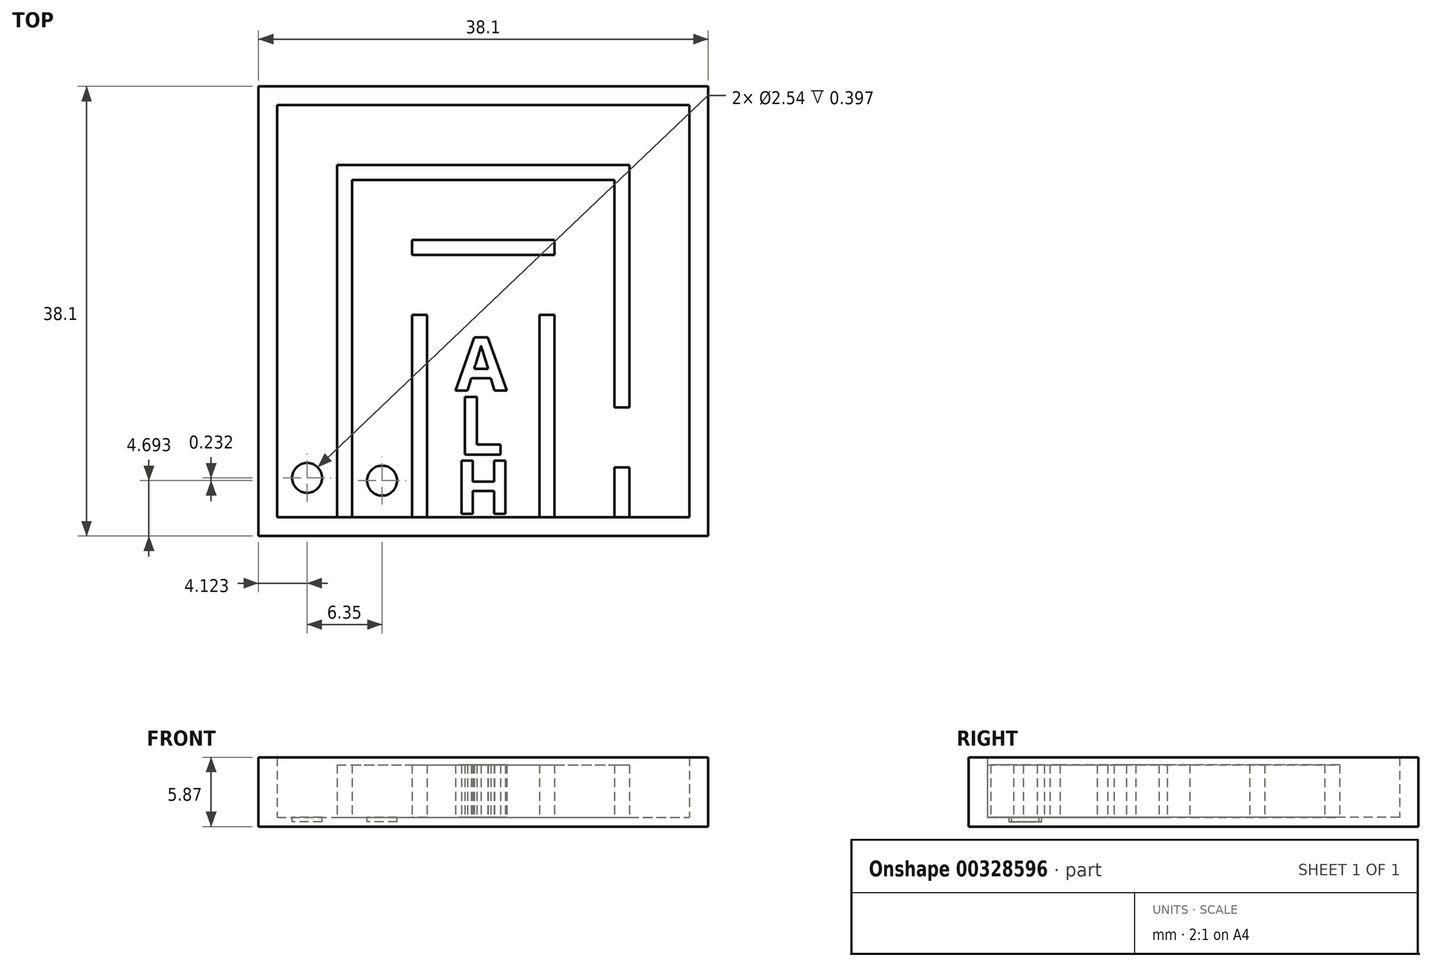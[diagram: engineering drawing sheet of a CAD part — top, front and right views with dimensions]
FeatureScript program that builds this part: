
annotation { "Feature Type Name" : "Feature", "Feature Type Description" : "" }
export const myFeature = defineFeature(function(context is Context, id is Id, definition is map)
    precondition{}
    {
        {
            var Q0;
            Q0=qCreatedBy(makeId("Top.planeOp"),FACE);
            var sketch = newSketch(context, id + "F0", { "sketchPlane" : qUnion([Q0])});
            skLineSegment(sketch, "E0.bottom", {"start": v(-17.72, 13.91) * mm, "end": v(20.38, 13.91) * mm});
            skLineSegment(sketch, "E0.top", {"start": v(-17.72, -24.19) * mm, "end": v(20.38, -24.19) * mm});
            skLineSegment(sketch, "E0.left", {"start": v(-17.72, 13.91) * mm, "end": v(-17.72, -24.19) * mm});
            skLineSegment(sketch, "E0.right", {"start": v(20.38, 13.91) * mm, "end": v(20.38, -24.19) * mm});
            skSolve(sketch);
        }
        {
            var Q0;
            Q0=makeQuery(id+"F0.imprint","IMPRINT",FACE,{"disambiguationData":[TD([[makeQuery(id+"F0.imprint","IMPRINT",EDGE,{"derivedFrom":sQuery(id+"F0.wireOp",EDGE,"E0.bottom")}),-1.0]])]});
            extrude(context, id + "F1", {"entities" : qUnion([Q0]), "depth" : 0.8 * mm});
        }
        {
            var Q0;
            Q0=makeQuery(id+"F1.opExtrude","CAP_FACE",FACE,{"disambiguationData":[OSD([sQuery(id+"F0.wireOp",EDGE,"E0.bottom"),sQuery(id+"F0.wireOp",EDGE,"E0.top"),sQuery(id+"F0.wireOp",EDGE,"E0.left"),sQuery(id+"F0.wireOp",EDGE,"E0.right")])],"isStart":false});
            var sketch = newSketch(context, id + "F2", { "sketchPlane" : qUnion([Q0])});
            skLineSegment(sketch, "E1.0", {"start": v(-16.14, 12.33) * mm, "end": v(18.79, 12.33) * mm});
            skLineSegment(sketch, "E1.1", {"start": v(-16.14, 12.33) * mm, "end": v(-16.14, -22.6) * mm});
            skLineSegment(sketch, "E1.2", {"start": v(-16.14, -22.6) * mm, "end": v(18.79, -22.6) * mm});
            skLineSegment(sketch, "E1.3", {"start": v(18.79, 12.33) * mm, "end": v(18.79, -22.6) * mm});
            skSolve(sketch);
        }
        {
            var Q0;
            Q0=makeQuery(id+"F2.imprint","IMPRINT",FACE,{"disambiguationData":[TD([[makeQuery(id+"F2.imprint","IMPRINT",EDGE,{"derivedFrom":sQuery(id+"F2.wireOp",EDGE,"E1.0")}),1.0]])]});
            extrude(context, id + "F3", {"entities" : qUnion([Q0]), "operationType" : NewBodyOperationType.ADD, "depth" : 5.08 * mm});
        }
        {
            var Q0;
            Q0=makeQuery(id+"F1.opExtrude","CAP_FACE",FACE,{"disambiguationData":[OSD([sQuery(id+"F0.wireOp",EDGE,"E0.bottom"),sQuery(id+"F0.wireOp",EDGE,"E0.top"),sQuery(id+"F0.wireOp",EDGE,"E0.left"),sQuery(id+"F0.wireOp",EDGE,"E0.right")])],"isStart":false});
            var sketch = newSketch(context, id + "F4", { "sketchPlane" : qUnion([Q0])});
            skLineSegment(sketch, "E2.bottom", {"start": v(-11.06, -22.6) * mm, "end": v(-9.79, -22.6) * mm});
            skLineSegment(sketch, "E2.top", {"start": v(-11.06, 7.25) * mm, "end": v(-9.79, 7.25) * mm});
            skLineSegment(sketch, "E2.left", {"start": v(-11.06, -22.6) * mm, "end": v(-11.06, 7.25) * mm});
            skLineSegment(sketch, "E2.right", {"start": v(-9.79, -22.6) * mm, "end": v(-9.79, 5.98) * mm});
            skLineSegment(sketch, "E3.bottom", {"start": v(-9.79, 7.25) * mm, "end": v(13.7, 7.25) * mm});
            skLineSegment(sketch, "E3.top", {"start": v(-9.79, 5.98) * mm, "end": v(12.44, 5.98) * mm});
            skLineSegment(sketch, "E3.right", {"start": v(13.7, 7.25) * mm, "end": v(13.7, 5.98) * mm});
            skLineSegment(sketch, "E4.left", {"start": v(18.79, 5.98) * mm, "end": v(18.79, 0.9) * mm});
            skLineSegment(sketch, "E5.right", {"start": v(7.36, -0.37) * mm, "end": v(7.36, 0.9) * mm});
            skLineSegment(sketch, "E6.top", {"start": v(12.44, -13.3) * mm, "end": v(13.7, -13.3) * mm});
            skLineSegment(sketch, "E6.left", {"start": v(12.44, 5.98) * mm, "end": v(12.44, -13.3) * mm});
            skLineSegment(sketch, "E6.right", {"start": v(13.7, 5.98) * mm, "end": v(13.7, -13.3) * mm});
            skLineSegment(sketch, "E7.bottom", {"start": v(12.44, -22.6) * mm, "end": v(13.7, -22.6) * mm});
            skLineSegment(sketch, "E7.top", {"start": v(12.44, -18.39) * mm, "end": v(13.7, -18.39) * mm});
            skLineSegment(sketch, "E7.left", {"start": v(12.44, -22.6) * mm, "end": v(12.44, -18.39) * mm});
            skLineSegment(sketch, "E7.right", {"start": v(13.7, -22.6) * mm, "end": v(13.7, -18.39) * mm});
            skLineSegment(sketch, "E8.bottom", {"start": v(-3.44, -22.6) * mm, "end": v(-4.7, -22.6) * mm});
            skLineSegment(sketch, "E8.top", {"start": v(-3.44, -5.45) * mm, "end": v(-4.7, -5.45) * mm});
            skLineSegment(sketch, "E8.left", {"start": v(-3.44, -22.6) * mm, "end": v(-3.44, -5.45) * mm});
            skLineSegment(sketch, "E8.right", {"start": v(-4.7, -22.6) * mm, "end": v(-4.7, -5.45) * mm});
            skLineSegment(sketch, "E9.trimOffspring", {"start": v(12.44, 5.98) * mm, "end": v(-0.53, 5.98) * mm});
            skLineSegment(sketch, "E10", {"start": v(-4.7, 0.9) * mm, "end": v(-4.7, -0.37) * mm});
            skLineSegment(sketch, "E11", {"start": v(-4.7, -0.37) * mm, "end": v(7.36, -0.37) * mm});
            skLineSegment(sketch, "E12", {"start": v(-4.7, 0.9) * mm, "end": v(7.36, 0.9) * mm});
            skLineSegment(sketch, "E13.bottom", {"start": v(6.09, -5.45) * mm, "end": v(7.36, -5.45) * mm});
            skLineSegment(sketch, "E13.top", {"start": v(6.09, -22.6) * mm, "end": v(7.36, -22.6) * mm});
            skLineSegment(sketch, "E13.left", {"start": v(6.09, -5.45) * mm, "end": v(6.09, -22.6) * mm});
            skLineSegment(sketch, "E13.right", {"start": v(7.36, -5.45) * mm, "end": v(7.36, -22.6) * mm});
            skLineSegment(sketch, "E14", {"start": v(-16.14, -22.6) * mm, "end": v(-11.06, -22.6) * mm});
            skCircle(sketch, "E15", {"center": v(-13.6, -19.26) * mm, "radius": 1.27 * mm});
            skPoint(sketch, "E15.centerSnap0", {"position": v(-13.6, -22.6) * mm});
            skLineSegment(sketch, "E16", {"start": v(-9.79, -22.6) * mm, "end": v(-4.7, -22.6) * mm});
            skCircle(sketch, "E17", {"center": v(-7.25, -19.5) * mm, "radius": 1.27 * mm});
            skPoint(sketch, "E17.centerSnap0", {"position": v(-7.25, -22.6) * mm});
            skSolve(sketch);
        }
        {
            var Q0;
            Q0=makeQuery(id+"F4.imprint","IMPRINT",FACE,{"disambiguationData":[TD([[makeQuery(id+"F4.imprint","IMPRINT",EDGE,{"derivedFrom":sQuery(id+"F4.wireOp",EDGE,"E2.bottom")}),1.0]])]});
            var Q1;
            Q1=makeQuery(id+"F4.imprint","IMPRINT",FACE,{"disambiguationData":[TD([[makeQuery(id+"F4.imprint","IMPRINT",EDGE,{"derivedFrom":sQuery(id+"F4.wireOp",EDGE,"E5.right")}),1.0]])]});
            var Q2;
            Q2=makeQuery(id+"F4.imprint","IMPRINT",FACE,{"disambiguationData":[TD([[makeQuery(id+"F4.imprint","IMPRINT",EDGE,{"derivedFrom":sQuery(id+"F4.wireOp",EDGE,"E8.bottom")}),1.0]])]});
            var Q3;
            Q3=makeQuery(id+"F4.imprint","IMPRINT",FACE,{"disambiguationData":[TD([[makeQuery(id+"F4.imprint","IMPRINT",EDGE,{"derivedFrom":sQuery(id+"F4.wireOp",EDGE,"E13.bottom")}),-1.0]])]});
            var Q4;
            Q4=makeQuery(id+"F4.imprint","IMPRINT",FACE,{"disambiguationData":[TD([[makeQuery(id+"F4.imprint","IMPRINT",EDGE,{"derivedFrom":sQuery(id+"F4.wireOp",EDGE,"E7.bottom")}),1.0]])]});
            var Q5;
            Q5=makeQuery(id+"F4.imprint","IMPRINT",FACE,{"disambiguationData":[TD([[makeQuery(id+"F4.imprint","IMPRINT",EDGE,{"derivedFrom":sQuery(id+"F4.wireOp",EDGE,"E6.top")}),1.0]])]});
            extrude(context, id + "F5", {"entities" : qUnion([Q0, Q1, Q2, Q3, Q4, Q5]), "operationType" : NewBodyOperationType.ADD, "depth" : 4.44 * mm});
        }
        {
            var Q0;
            Q0=makeQuery(id+"F4.imprint","IMPRINT",FACE,{"disambiguationData":[TD([[makeQuery(id+"F4.imprint","IMPRINT",EDGE,{"derivedFrom":sQuery(id+"F4.wireOp",EDGE,"E15")}),1.0]])]});
            var Q1;
            Q1=makeQuery(id+"F4.imprint","IMPRINT",FACE,{"disambiguationData":[TD([[makeQuery(id+"F4.imprint","IMPRINT",EDGE,{"derivedFrom":sQuery(id+"F4.wireOp",EDGE,"E17")}),1.0]])]});
            extrude(context, id + "F6", {"entities" : qUnion([Q0, Q1]), "operationType" : NewBodyOperationType.REMOVE, "oppositeDirection" : true, "depth" : 0.4 * mm});
        }
        {
            var Q0;
            Q0=makeQuery(id+"F4.imprint","IMPRINT",FACE,{"disambiguationData":[TD([[makeQuery(id+"F4.imprint","IMPRINT",EDGE,{"derivedFrom":sQuery(id+"F4.wireOp",EDGE,"E2.top")}),1.0]])]});
            var sketch = newSketch(context, id + "F7", { "sketchPlane" : qUnion([Q0])});
            skText(sketch, "E18", { "text": "A", "fontName": "OpenSans-Bold.ttf"});
            const initialGuessF7  = {"E18": [-0.00103, -0.01188, 1, 0, 0.00453]};
            skSetInitialGuess(sketch, initialGuessF7);
            skSolve(sketch);
        }
        {
            var Q0;
            Q0 = qSketchRegion(id + "F7", true);
            extrude(context, id + "F8", {"entities" : qUnion([Q0]), "operationType" : NewBodyOperationType.ADD, "depth" : 4.44 * mm});
        }
        {
            var Q0;
            Q0=makeQuery(id+"F4.imprint","IMPRINT",FACE,{"disambiguationData":[TD([[makeQuery(id+"F4.imprint","IMPRINT",EDGE,{"derivedFrom":sQuery(id+"F4.wireOp",EDGE,"E2.top")}),1.0]])]});
            var sketch = newSketch(context, id + "F9", { "sketchPlane" : qUnion([Q0])});
            skText(sketch, "E19", { "text": "L", "fontName": "OpenSans-Bold.ttf"});
            const initialGuessF9  = {"E19": [-0.00085, -0.01729, 1, 0, 0.00492]};
            skSetInitialGuess(sketch, initialGuessF9);
            skSolve(sketch);
        }
        {
            var Q0;
            Q0=makeQuery(id+"F4.imprint","IMPRINT",FACE,{"disambiguationData":[TD([[makeQuery(id+"F4.imprint","IMPRINT",EDGE,{"derivedFrom":sQuery(id+"F4.wireOp",EDGE,"E2.top")}),1.0]])]});
            var sketch = newSketch(context, id + "F10", { "sketchPlane" : qUnion([Q0])});
            skText(sketch, "E20", { "text": "H", "fontName": "OpenSans-Bold.ttf"});
            const initialGuessF10  = {"E20": [-0.00108, -0.02232, 1, 0, 0.00457]};
            skSetInitialGuess(sketch, initialGuessF10);
            skSolve(sketch);
        }
        {
            var Q0;
            Q0 = qSketchRegion(id + "F9", true);
            var Q1;
            Q1 = qSketchRegion(id + "F10", true);
            extrude(context, id + "F11", {"entities" : qUnion([Q0, Q1]), "operationType" : NewBodyOperationType.ADD, "depth" : 4.44 * mm});
        }
    });
